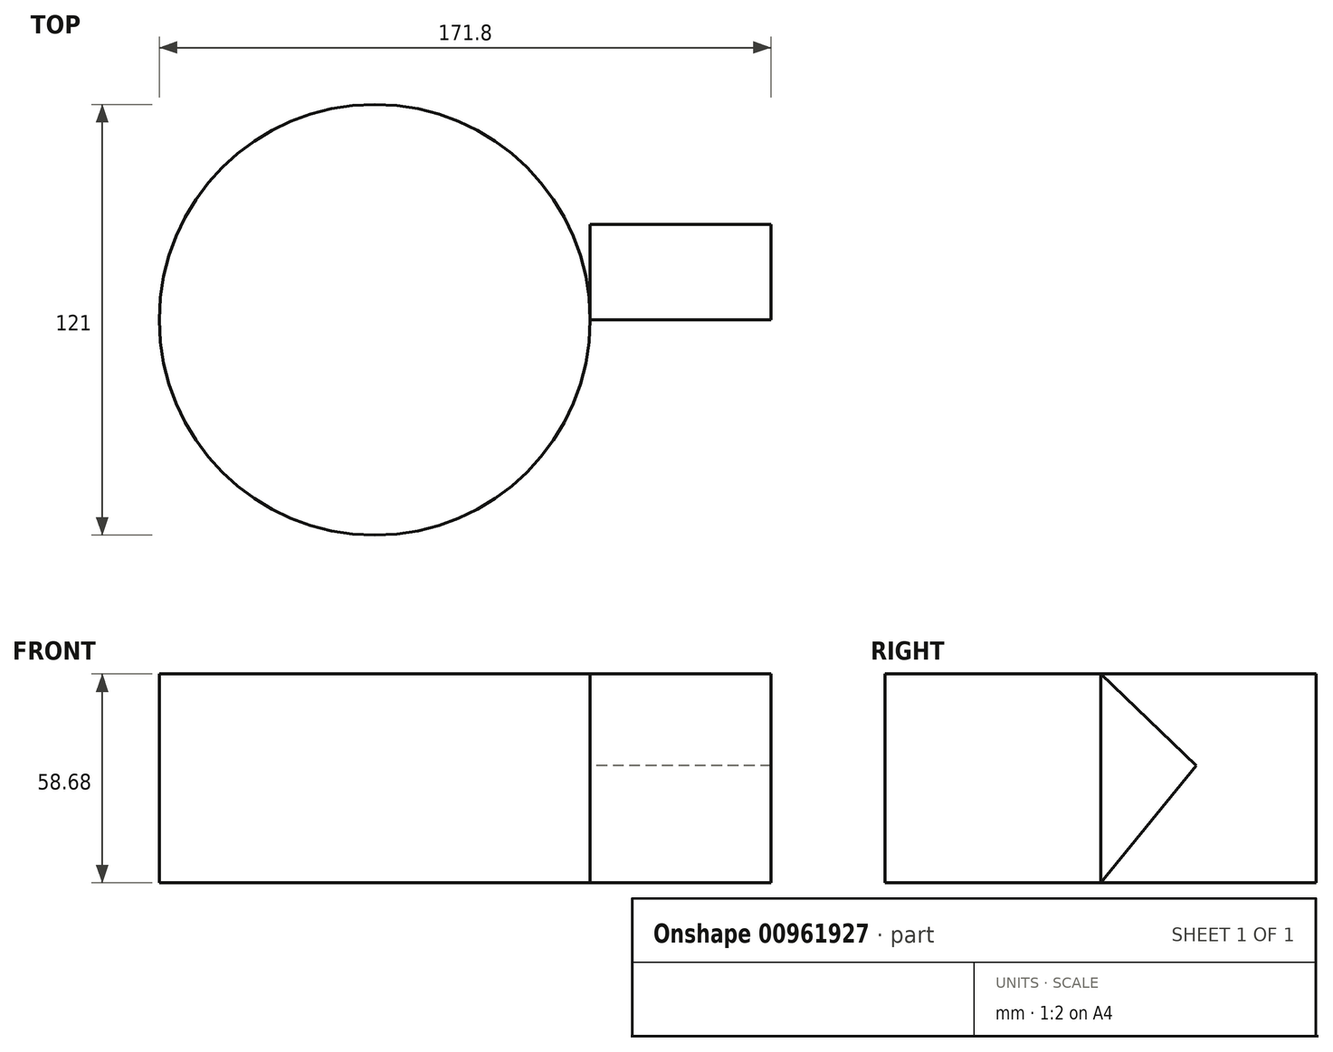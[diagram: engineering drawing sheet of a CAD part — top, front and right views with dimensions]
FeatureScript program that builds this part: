
annotation { "Feature Type Name" : "Feature", "Feature Type Description" : "" }
export const myFeature = defineFeature(function(context is Context, id is Id, definition is map)
    precondition{}
    {
        {
            var Q0;
            Q0=qCreatedBy(makeId("Right.planeOp"),FACE);
            var sketch = newSketch(context, id + "F0", { "sketchPlane" : qUnion([Q0])});
            skLineSegment(sketch, "E0", {"start": v(0, 0) * mm, "end": v(-26.81, 25.69) * mm});
            skLineSegment(sketch, "E1", {"start": v(-26.81, 25.69) * mm, "end": v(-26.81, -32.99) * mm});
            skLineSegment(sketch, "E2", {"start": v(-26.81, -32.99) * mm, "end": v(0, 0) * mm});
            skSolve(sketch);
        }
        {
            var Q0;
            Q0 = qSketchRegion(id + "F0", true);
            extrude(context, id + "F1", {"entities" : qUnion([Q0]), "depth" : 50.8 * mm, "offsetDistance" : 25.4 * mm});
        }
        {
            var Q0;
            Q0=makeQuery(id+"F1.opExtrude","SWEPT_FACE",FACE,{"disambiguationData":[OSD([sQuery(id+"F0.wireOp",EDGE,"E1")])]});
            var sketch = newSketch(context, id + "F2", { "sketchPlane" : qUnion([Q0])});
            skLineSegment(sketch, "E3", {"start": v(0, -32.99) * mm, "end": v(-60.5, -32.99) * mm});
            skLineSegment(sketch, "E4.bottom", {"start": v(-60.5, -32.99) * mm, "end": v(0, -32.99) * mm});
            skLineSegment(sketch, "E4.top", {"start": v(-60.5, 25.69) * mm, "end": v(0, 25.69) * mm});
            skLineSegment(sketch, "E4.left", {"start": v(-60.5, -32.99) * mm, "end": v(-60.5, 25.69) * mm});
            skLineSegment(sketch, "E4.right", {"start": v(0, -32.99) * mm, "end": v(0, 25.69) * mm});
            skSolve(sketch);
        }
        {
            var Q0;
            Q0 = qSketchRegion(id + "F2", true);
            var Q1;
            Q1=sQuery(id+"F2.wireOp",EDGE,"E4.left");
            revolve(context, id + "F3", {"surfaceOperationType" : NewSurfaceOperationType.NEW, "entities" : qUnion([Q0]), "axis" : qUnion([Q1]), "revolveType" : RevolveType.FULL});
        }
    });
